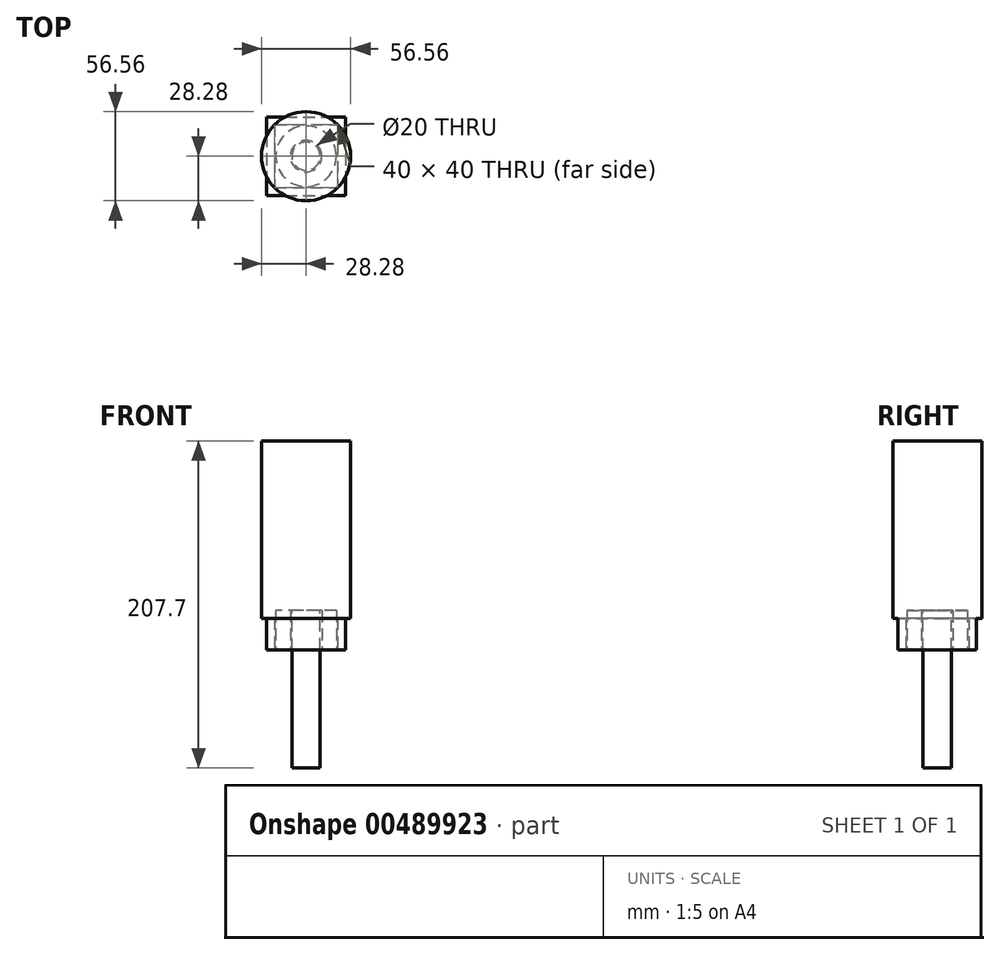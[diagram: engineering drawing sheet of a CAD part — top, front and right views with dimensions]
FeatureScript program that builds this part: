
annotation { "Feature Type Name" : "Feature", "Feature Type Description" : "" }
export const myFeature = defineFeature(function(context is Context, id is Id, definition is map)
    precondition{}
    {
        {
            var Q0;
            Q0=qCreatedBy(makeId("Top.planeOp"),FACE);
            var sketch = newSketch(context, id + "F0", { "sketchPlane" : qUnion([Q0])});
            skLineSegment(sketch, "E0.bottom", {"start": v(-20, 20) * mm, "end": v(20, 20) * mm});
            skLineSegment(sketch, "E0.top", {"start": v(-20, -20) * mm, "end": v(20, -20) * mm});
            skLineSegment(sketch, "E0.left", {"start": v(-20, 20) * mm, "end": v(-20, -20) * mm});
            skLineSegment(sketch, "E0.right", {"start": v(20, 20) * mm, "end": v(20, -20) * mm});
            skPoint(sketch, "E0.middle", {"position": v(0, 0) * mm});
            skLineSegment(sketch, "E1.bottom", {"start": v(-25, 25) * mm, "end": v(25, 25) * mm});
            skLineSegment(sketch, "E1.top", {"start": v(-25, -25) * mm, "end": v(25, -25) * mm});
            skLineSegment(sketch, "E1.left", {"start": v(-25, 25) * mm, "end": v(-25, -25) * mm});
            skLineSegment(sketch, "E1.right", {"start": v(25, 25) * mm, "end": v(25, -25) * mm});
            skCircle(sketch, "E2", {"center": v(0, 0) * mm, "radius": 19.25 * mm});
            skCircle(sketch, "E3", {"center": v(0, 0) * mm, "radius": 10 * mm});
            skSolve(sketch);
        }
        {
            var Q0;
            Q0=makeQuery(id+"F0.imprint","IMPRINT",FACE,{"disambiguationData":[TD([[makeQuery(id+"F0.imprint","IMPRINT",EDGE,{"derivedFrom":sQuery(id+"F0.wireOp",EDGE,"E2")}),1.0]])]});
            extrude(context, id + "F1", {"entities" : qUnion([Q0]), "depth" : 25 * mm});
        }
        {
            var Q0;
            Q0=qSketchRegion(id+"F0",true);
            extrude(context, id + "F2", {"entities" : qUnion([Q0]), "depth" : 20 * mm});
        }
        {
            var Q0;
            Q0=makeQuery(id+"F1.opExtrude","CAP_FACE",FACE,{"disambiguationData":[OSD([sQuery(id+"F0.wireOp",EDGE,"E2"),sQuery(id+"F0.wireOp",EDGE,"E3")])],"isStart":false});
            var sketch = newSketch(context, id + "F3", { "sketchPlane" : qUnion([Q0])});
            skCircle(sketch, "E4", {"center": v(0, 0) * mm, "radius": 9 * mm});
            skSolve(sketch);
        }
        {
            var Q0;
            Q0=makeQuery(id+"F3.imprint","IMPRINT",FACE,{"disambiguationData":[TD([[makeQuery(id+"F3.imprint","IMPRINT",EDGE,{"derivedFrom":sQuery(id+"F3.wireOp",EDGE,"E4")}),1.0]])]});
            extrude(context, id + "F4", {"entities" : qUnion([Q0]), "oppositeDirection" : true, "depth" : 100 * mm});
        }
        {
            var Q0;
            Q0=makeQuery(id+"F2.opExtrude","CAP_FACE",FACE,{"disambiguationData":[OSD([sQuery(id+"F0.wireOp",EDGE,"E0.bottom"),sQuery(id+"F0.wireOp",EDGE,"E0.top"),sQuery(id+"F0.wireOp",EDGE,"E0.left"),sQuery(id+"F0.wireOp",EDGE,"E0.right"),sQuery(id+"F0.wireOp",EDGE,"E1.bottom"),sQuery(id+"F0.wireOp",EDGE,"E1.top"),sQuery(id+"F0.wireOp",EDGE,"E1.left"),sQuery(id+"F0.wireOp",EDGE,"E1.right")])],"isStart":false});
            var sketch = newSketch(context, id + "F5", { "sketchPlane" : qUnion([Q0])});
            skCircle(sketch, "E5", {"center": v(0, 0) * mm, "radius": 28.28 * mm});
            skSolve(sketch);
        }
        {
            var Q0;
            Q0=makeQuery(id+"F5.imprint","IMPRINT",FACE,{"disambiguationData":[TD([[makeQuery(id+"F5.imprint","IMPRINT",EDGE,{"derivedFrom":makeQuery(id+"F2.opExtrude","CAP_EDGE",EDGE,{"disambiguationData":[OSD([sQuery(id+"F0.wireOp",EDGE,"E0.bottom")])],"isStart":false})}),-1.0]])]});
            var Q1;
            {var subQ1=makeQuery(id+"F2.opExtrude","CAP_EDGE",EDGE,{"disambiguationData":[OSD([sQuery(id+"F0.wireOp",EDGE,"E0.right")])],"isStart":false});Q1=makeQuery(id+"F5.imprint","IMPRINT",FACE,{"disambiguationData":[TD([[makeQuery(id+"F5.imprint","IMPRINT",EDGE,{"derivedFrom":subQ1}),1.0]])]});}
            var Q2;
            {var subQ1=makeQuery(id+"F2.opExtrude","CAP_EDGE",EDGE,{"disambiguationData":[OSD([sQuery(id+"F0.wireOp",EDGE,"E0.bottom")])],"isStart":false});Q2=makeQuery(id+"F5.imprint","IMPRINT",FACE,{"disambiguationData":[TD([[makeQuery(id+"F5.imprint","IMPRINT",EDGE,{"derivedFrom":subQ1}),1.0]])]});}
            var Q3;
            {var subQ0=sQuery(id+"F5.wireOp",EDGE,"E5");var subQ1=makeQuery(id+"F2.opExtrude","CAP_EDGE",EDGE,{"disambiguationData":[OSD([sQuery(id+"F0.wireOp",EDGE,"E1.bottom")])],"isStart":false});var subQ2=makeQuery(id+"F5.imprint","INTERSECT",VERTEX,{"disambiguationData":[OD(0.0)],"derivedFrom":[subQ1,subQ0]});Q3=makeQuery(id+"F5.imprint","IMPRINT",FACE,{"disambiguationData":[TD([[makeQuery(id+"F5.imprint","IMPRINT",EDGE,{"disambiguationData":[TD([[subQ2,-1.0]])],"derivedFrom":subQ0}),1.0]])]});}
            var Q4;
            {var subQ1=makeQuery(id+"F2.opExtrude","CAP_EDGE",EDGE,{"disambiguationData":[OSD([sQuery(id+"F0.wireOp",EDGE,"E0.left")])],"isStart":false});Q4=makeQuery(id+"F5.imprint","IMPRINT",FACE,{"disambiguationData":[TD([[makeQuery(id+"F5.imprint","IMPRINT",EDGE,{"derivedFrom":subQ1}),-1.0]])]});}
            var Q5;
            {var subQ0=sQuery(id+"F5.wireOp",EDGE,"E5");var subQ1=makeQuery(id+"F2.opExtrude","CAP_EDGE",EDGE,{"disambiguationData":[OSD([sQuery(id+"F0.wireOp",EDGE,"E1.left")])],"isStart":false});var subQ2=makeQuery(id+"F5.imprint","INTERSECT",VERTEX,{"disambiguationData":[OD(0.0)],"derivedFrom":[subQ1,subQ0]});Q5=makeQuery(id+"F5.imprint","IMPRINT",FACE,{"disambiguationData":[TD([[makeQuery(id+"F5.imprint","IMPRINT",EDGE,{"disambiguationData":[TD([[subQ2,-1.0]])],"derivedFrom":subQ0}),1.0]])]});}
            var Q6;
            {var subQ0=sQuery(id+"F5.wireOp",EDGE,"E5");var subQ1=makeQuery(id+"F2.opExtrude","CAP_EDGE",EDGE,{"disambiguationData":[OSD([sQuery(id+"F0.wireOp",EDGE,"E1.top")])],"isStart":false});var subQ2=makeQuery(id+"F5.imprint","INTERSECT",VERTEX,{"disambiguationData":[OD(0.0)],"derivedFrom":[subQ1,subQ0]});Q6=makeQuery(id+"F5.imprint","IMPRINT",FACE,{"disambiguationData":[TD([[makeQuery(id+"F5.imprint","IMPRINT",EDGE,{"disambiguationData":[TD([[subQ2,-1.0]])],"derivedFrom":subQ0}),1.0]])]});}
            var Q7;
            {var subQ1=makeQuery(id+"F2.opExtrude","CAP_EDGE",EDGE,{"disambiguationData":[OSD([sQuery(id+"F0.wireOp",EDGE,"E0.top")])],"isStart":false});Q7=makeQuery(id+"F5.imprint","IMPRINT",FACE,{"disambiguationData":[TD([[makeQuery(id+"F5.imprint","IMPRINT",EDGE,{"derivedFrom":subQ1}),-1.0]])]});}
            var Q8;
            {var subQ0=sQuery(id+"F5.wireOp",EDGE,"E5");var subQ1=makeQuery(id+"F2.opExtrude","CAP_EDGE",EDGE,{"disambiguationData":[OSD([sQuery(id+"F0.wireOp",EDGE,"E1.right")])],"isStart":false});var subQ2=makeQuery(id+"F5.imprint","INTERSECT",VERTEX,{"disambiguationData":[OD(0.0)],"derivedFrom":[subQ1,subQ0]});Q8=makeQuery(id+"F5.imprint","IMPRINT",FACE,{"disambiguationData":[TD([[makeQuery(id+"F5.imprint","IMPRINT",EDGE,{"disambiguationData":[TD([[subQ2,1.0]])],"derivedFrom":subQ0}),1.0]])]});}
            extrude(context, id + "F6", {"entities" : qUnion([Q0, Q1, Q2, Q3, Q4, Q5, Q6, Q7, Q8]), "depth" : 112.7 * mm});
        }
    });
